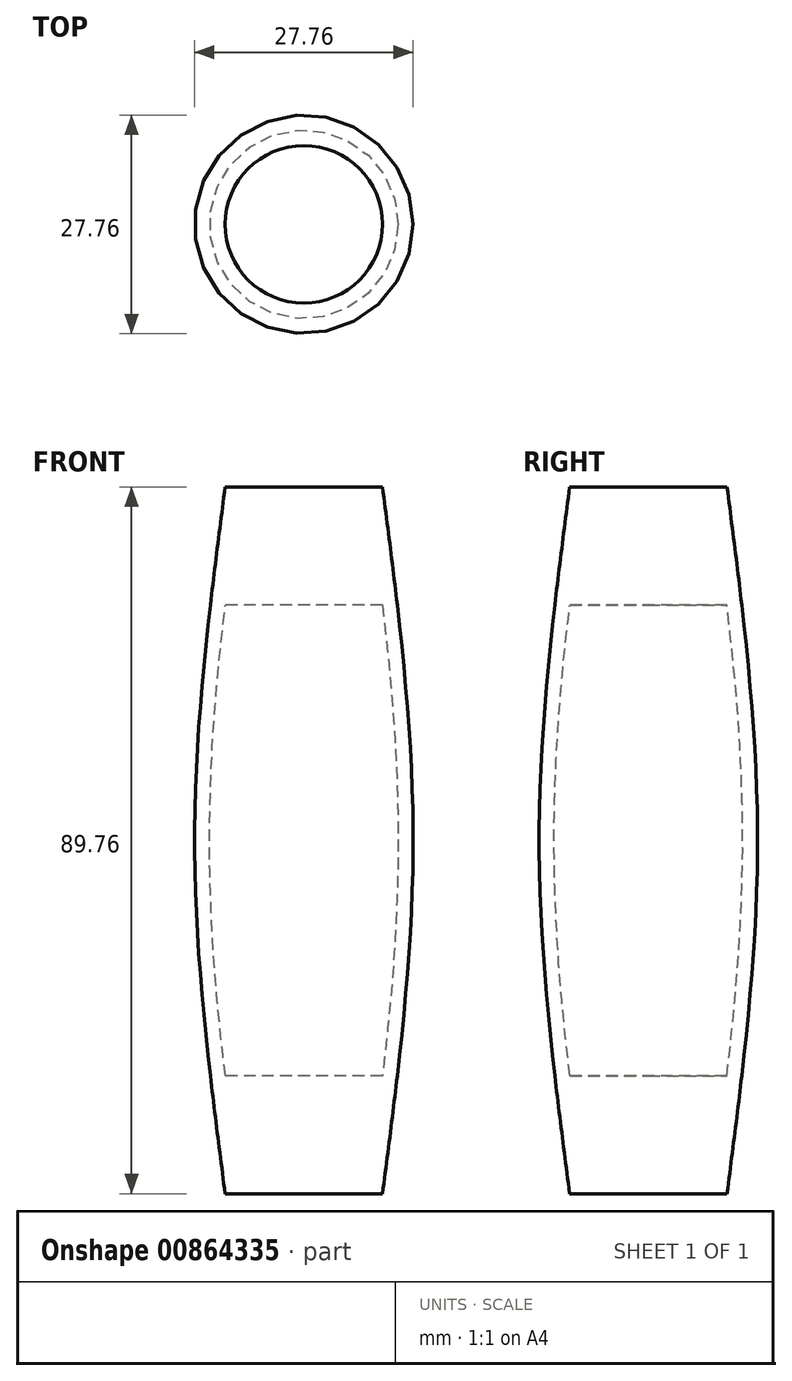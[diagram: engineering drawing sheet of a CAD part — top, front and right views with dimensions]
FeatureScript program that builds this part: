
annotation { "Feature Type Name" : "Feature", "Feature Type Description" : "" }
export const myFeature = defineFeature(function(context is Context, id is Id, definition is map)
    precondition{}
    {
        {
            var Q0;
            Q0=qCreatedBy(makeId("Front.planeOp"),FACE);
            var sketch = newSketch(context, id + "F0", { "sketchPlane" : qUnion([Q0])});
            skLineSegment(sketch, "E0", {"start": v(0, 44.88) * mm, "end": v(-10, 44.88) * mm});
            skLineSegment(sketch, "E1.MirrorCS", {"start": v(0, -44.88) * mm, "end": v(-10, -44.88) * mm});
            skFitSpline(sketch, "E2", {"points": [v(-10, 44.88) * mm, v(-13.87, 0) * mm, v(-10, -44.88) * mm], "startDerivative": vector(-11.62, -89.76) * mm, "endDerivative": vector(11.63, -89.76) * mm});
            skLineSegment(sketch, "E3", {"start": v(0, 44.88) * mm, "end": v(0, -44.88) * mm, "construction": true});
            skLineSegment(sketch, "E4", {"start": v(0, 44.88) * mm, "end": v(0, -44.88) * mm});
            skLineSegment(sketch, "E5", {"start": v(0, 29.92) * mm, "end": v(-11.94, 29.92) * mm});
            skLineSegment(sketch, "E6", {"start": v(-11.94, -29.92) * mm, "end": v(0, -29.92) * mm});
            skFitSpline(sketch, "E7.0", {"points": [v(-8.1, 44.63) * mm, v(-8.58, 40.9) * mm, v(-9.55, 33.42) * mm, v(-10.81, 22.25) * mm, v(-11.57, 12.96) * mm, v(-11.9, 5.55) * mm, v(-11.98, 0) * mm, v(-11.9, -5.55) * mm, v(-11.57, -12.96) * mm, v(-10.81, -22.25) * mm, v(-9.55, -33.42) * mm, v(-8.58, -40.9) * mm, v(-8.1, -44.63) * mm]});
            skSolve(sketch);
        }
        {
            var Q0;
            {var subQ5=sQuery(id+"F0.wireOp",EDGE,"E0");Q0=makeQuery(id+"F0.imprint","IMPRINT",FACE,{"disambiguationData":[TD([[makeQuery(id+"F0.imprint","IMPRINT",EDGE,{"derivedFrom":subQ5}),1.0]])]});}
            var Q1;
            {var subQ0=sQuery(id+"F0.wireOp",EDGE,"E5");var subQ1=sQuery(id+"F0.wireOp",EDGE,"E2");var subQ2=makeQuery(id+"F0.imprint","INTERSECT",VERTEX,{"derivedFrom":[subQ1,subQ0]});Q1=makeQuery(id+"F0.imprint","IMPRINT",FACE,{"disambiguationData":[TD([[makeQuery(id+"F0.imprint","IMPRINT",EDGE,{"disambiguationData":[TD([[subQ2,-1.0]])],"derivedFrom":subQ1}),1.0]])]});}
            var Q2;
            {var subQ5=sQuery(id+"F0.wireOp",EDGE,"E1.MirrorCS");Q2=makeQuery(id+"F0.imprint","IMPRINT",FACE,{"disambiguationData":[TD([[makeQuery(id+"F0.imprint","IMPRINT",EDGE,{"derivedFrom":subQ5}),-1.0]])]});}
            var Q3;
            Q3=sQuery(id+"F0.wireOp",EDGE,"E4");
            revolve(context, id + "F1", {"surfaceOperationType" : NewSurfaceOperationType.NEW, "entities" : qUnion([Q0, Q1, Q2]), "axis" : qUnion([Q3]), "revolveType" : RevolveType.FULL});
        }
    });
